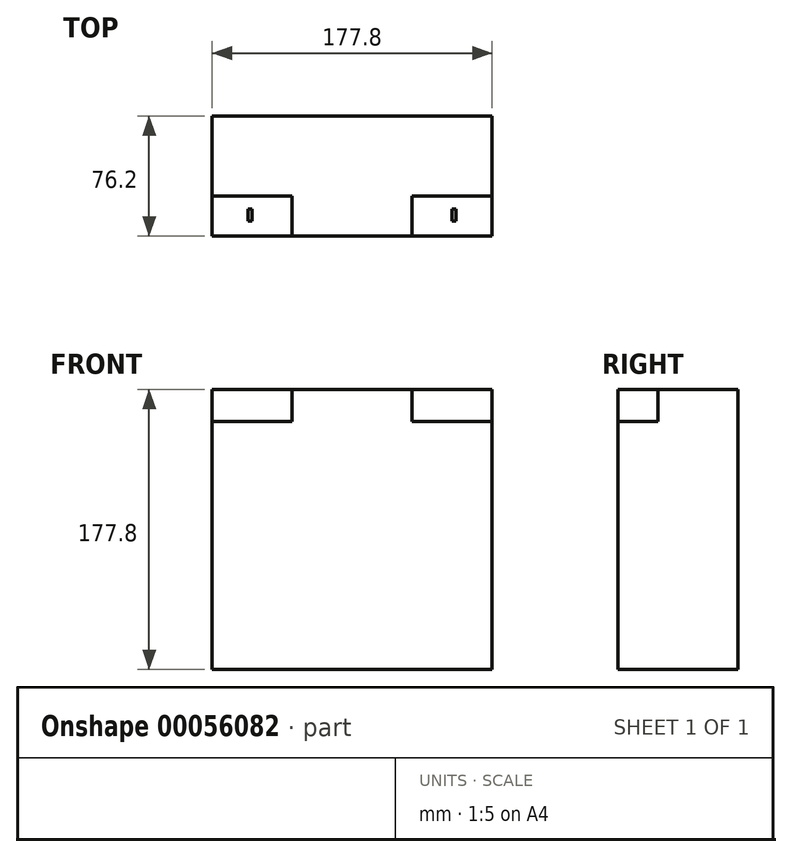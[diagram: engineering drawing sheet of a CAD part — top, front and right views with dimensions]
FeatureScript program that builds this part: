
annotation { "Feature Type Name" : "Feature", "Feature Type Description" : "" }
export const myFeature = defineFeature(function(context is Context, id is Id, definition is map)
    precondition{}
    {
        {
            var Q0;
            Q0=qCreatedBy(makeId("Top.planeOp"),FACE);
            var sketch = newSketch(context, id + "F0", { "sketchPlane" : qUnion([Q0])});
            skLineSegment(sketch, "E0", {"start": v(-106.16, 92.63) * mm, "end": v(-106.16, 16.43) * mm});
            skLineSegment(sketch, "E1", {"start": v(-106.16, 16.43) * mm, "end": v(71.64, 16.43) * mm});
            skLineSegment(sketch, "E2", {"start": v(71.64, 16.43) * mm, "end": v(71.64, 92.63) * mm});
            skLineSegment(sketch, "E3", {"start": v(71.64, 92.63) * mm, "end": v(-106.16, 92.63) * mm});
            skSolve(sketch);
        }
        {
            var Q0;
            Q0=makeQuery(id+"F0.imprint","IMPRINT",FACE,{"disambiguationData":[TD([[makeQuery(id+"F0.imprint","IMPRINT",EDGE,{"derivedFrom":sQuery(id+"F0.wireOp",EDGE,"E0")}),1.0]])]});
            extrude(context, id + "F1", {"entities" : qUnion([Q0]), "depth" : 177.8 * mm});
        }
        {
            var Q0;
            Q0=makeQuery(id+"F1.opExtrude","CAP_FACE",FACE,{"disambiguationData":[OSD([sQuery(id+"F0.wireOp",EDGE,"E0"),sQuery(id+"F0.wireOp",EDGE,"E1"),sQuery(id+"F0.wireOp",EDGE,"E2"),sQuery(id+"F0.wireOp",EDGE,"E3")])],"isStart":false});
            var sketch = newSketch(context, id + "F2", { "sketchPlane" : qUnion([Q0])});
            skLineSegment(sketch, "E4", {"start": v(-106.16, 41.83) * mm, "end": v(-55.36, 41.83) * mm});
            skLineSegment(sketch, "E5", {"start": v(-55.36, 41.83) * mm, "end": v(-55.36, 16.43) * mm});
            skLineSegment(sketch, "E6", {"start": v(-55.36, 16.43) * mm, "end": v(-106.16, 16.43) * mm});
            skLineSegment(sketch, "E7", {"start": v(-106.16, 16.43) * mm, "end": v(-106.16, 41.83) * mm});
            skLineSegment(sketch, "E8", {"start": v(71.64, 41.83) * mm, "end": v(20.84, 41.83) * mm});
            skLineSegment(sketch, "E9", {"start": v(20.84, 41.83) * mm, "end": v(20.84, 16.43) * mm});
            skLineSegment(sketch, "E10", {"start": v(20.84, 16.43) * mm, "end": v(71.64, 16.43) * mm});
            skLineSegment(sketch, "E11", {"start": v(71.64, 16.43) * mm, "end": v(71.64, 41.83) * mm});
            skSolve(sketch);
        }
        {
            var Q0;
            Q0 = qSketchRegion(id + "F2", true);
            extrude(context, id + "F3", {"entities" : qUnion([Q0]), "operationType" : NewBodyOperationType.REMOVE, "oppositeDirection" : true, "depth" : 20.32 * mm});
        }
        {
            var Q0;
            Q0=makeQuery(id+"F3.boolean.opBoolean","COPY",FACE,{"derivedFrom":makeQuery(id+"F3.opExtrude","CAP_FACE",FACE,{"disambiguationData":[OSD([sQuery(id+"F2.wireOp",EDGE,"E4"),sQuery(id+"F2.wireOp",EDGE,"E5"),sQuery(id+"F2.wireOp",EDGE,"E6"),sQuery(id+"F2.wireOp",EDGE,"E7")])],"isStart":false})});
            var sketch = newSketch(context, id + "F4", { "sketchPlane" : qUnion([Q0])});
            skLineSegment(sketch, "E12.bottom", {"start": v(-83.35, 33.56) * mm, "end": v(-80.76, 33.56) * mm});
            skLineSegment(sketch, "E12.top", {"start": v(-83.35, 25.95) * mm, "end": v(-80.76, 25.95) * mm});
            skLineSegment(sketch, "E12.left", {"start": v(-83.35, 33.56) * mm, "end": v(-83.35, 25.95) * mm});
            skLineSegment(sketch, "E12.right", {"start": v(-80.76, 33.56) * mm, "end": v(-80.76, 25.95) * mm});
            skSolve(sketch);
        }
        {
            var Q0;
            Q0=makeQuery(id+"F4.imprint","IMPRINT",FACE,{"disambiguationData":[TD([[makeQuery(id+"F4.imprint","IMPRINT",EDGE,{"derivedFrom":sQuery(id+"F4.wireOp",EDGE,"E12.bottom")}),-1.0]])]});
            extrude(context, id + "F5", {"entities" : qUnion([Q0]), "depth" : 3 / 101.6 * mm});
        }
        {
            var Q0;
            Q0=makeQuery(id+"F1.opExtrude","SWEPT_FACE",FACE,{"disambiguationData":[OSD([sQuery(id+"F0.wireOp",EDGE,"E0")])]});
            var Q1;
            Q1=makeQuery(id+"F1.opExtrude","SWEPT_FACE",FACE,{"disambiguationData":[OSD([sQuery(id+"F0.wireOp",EDGE,"E2")])]});
            cPlane(context, id + "F6", {"entities" : qUnion([Q0, Q1]), "cplaneType" : CPlaneType.MID_PLANE, "offset" : 152.4 * mm, "width" : 152.4 * mm, "height" : 152.4 * mm});
        }
        {
            var Q0;
            Q0=makeQuery(id+"F5.opExtrude","SWEPT_BODY",BODY,{"disambiguationData":[OSD([sQuery(id+"F4.wireOp",EDGE,"E12.bottom"),sQuery(id+"F4.wireOp",EDGE,"E12.top"),sQuery(id+"F4.wireOp",EDGE,"E12.left"),sQuery(id+"F4.wireOp",EDGE,"E12.right")])]});
            var Q1;
            Q1=qCreatedBy(id+"F6.planeOp",FACE);
            mirror(context, id + "F7", {"operationType" : NewBodyOperationType.ADD, "entities" : qUnion([Q0]), "mirrorPlane" : qUnion([Q1])});
        }
    });
